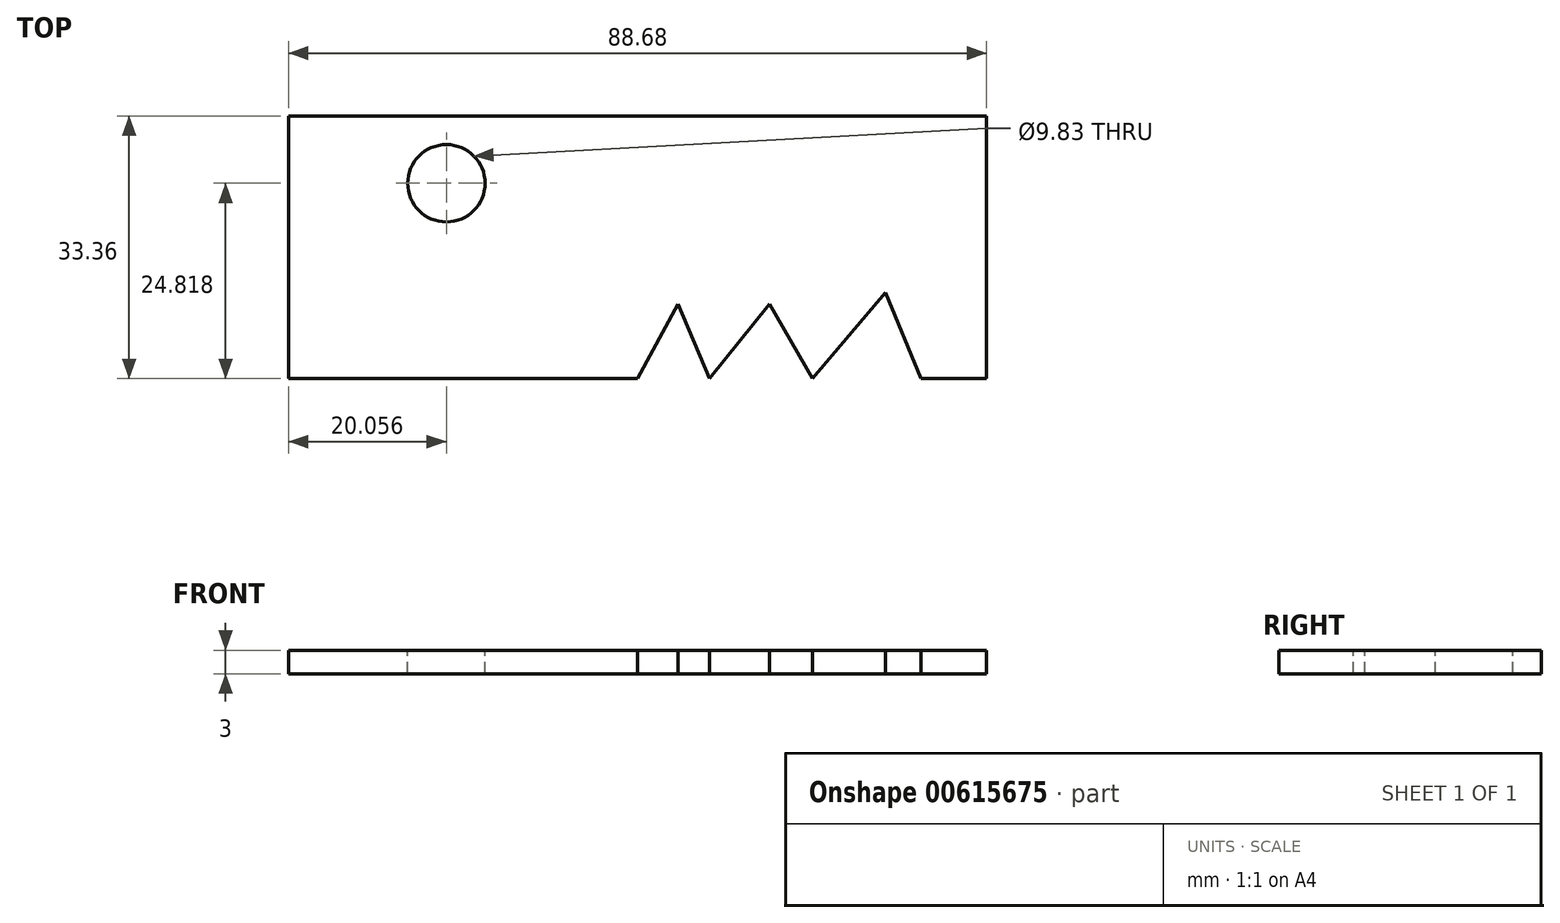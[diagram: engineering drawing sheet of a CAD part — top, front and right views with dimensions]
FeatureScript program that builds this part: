
annotation { "Feature Type Name" : "Feature", "Feature Type Description" : "" }
export const myFeature = defineFeature(function(context is Context, id is Id, definition is map)
    precondition{}
    {
        {
            var Q0;
            Q0=qCreatedBy(makeId("Top.planeOp"),FACE);
            var sketch = newSketch(context, id + "F0", { "sketchPlane" : qUnion([Q0])});
            skLineSegment(sketch, "E0.bottom", {"start": v(-44.34, 16.68) * mm, "end": v(44.34, 16.68) * mm});
            skLineSegment(sketch, "E0.top", {"start": v(-44.34, -16.68) * mm, "end": v(44.34, -16.68) * mm});
            skLineSegment(sketch, "E0.left", {"start": v(-44.34, 16.68) * mm, "end": v(-44.34, -16.68) * mm});
            skLineSegment(sketch, "E0.right", {"start": v(44.34, 16.68) * mm, "end": v(44.34, -16.68) * mm});
            skPoint(sketch, "E0.middle", {"position": v(0, 0) * mm});
            skSolve(sketch);
        }
        {
            var Q0;
            Q0 = qSketchRegion(id + "F0", true);
            extrude(context, id + "F1", {"entities" : qUnion([Q0]), "depth" : 3 * mm, "offsetDistance" : 25 * mm});
        }
        {
            var Q0;
            Q0=makeQuery(id+"F1.opExtrude","CAP_FACE",FACE,{"disambiguationData":[OSD([sQuery(id+"F0.wireOp",EDGE,"E0.bottom"),sQuery(id+"F0.wireOp",EDGE,"E0.top"),sQuery(id+"F0.wireOp",EDGE,"E0.left"),sQuery(id+"F0.wireOp",EDGE,"E0.right")])],"isStart":false});
            var sketch = newSketch(context, id + "F2", { "sketchPlane" : qUnion([Q0])});
            skCircle(sketch, "E1", {"center": v(-24.28, 8.14) * mm, "radius": 4.91 * mm});
            skPoint(sketch, "E1.first.point", {"position": v(-28.94, 9.7) * mm});
            skPoint(sketch, "E1.second.point", {"position": v(-19.5, 6.99) * mm});
            skPoint(sketch, "E1.third.point", {"position": v(-27.3, 4.26) * mm});
            skSolve(sketch);
        }
        {
            var Q0;
            Q0=makeQuery(id+"F2.imprint","IMPRINT",FACE,{"disambiguationData":[TD([[makeQuery(id+"F2.imprint","IMPRINT",EDGE,{"derivedFrom":sQuery(id+"F2.wireOp",EDGE,"E1")}),1.0]])]});
            extrude(context, id + "F3", {"entities" : qUnion([Q0]), "operationType" : NewBodyOperationType.REMOVE, "oppositeDirection" : true, "depth" : 25 * mm, "offsetDistance" : 25 * mm});
        }
        {
            var Q0;
            Q0=makeQuery(id+"F1.opExtrude","CAP_FACE",FACE,{"disambiguationData":[OSD([sQuery(id+"F0.wireOp",EDGE,"E0.bottom"),sQuery(id+"F0.wireOp",EDGE,"E0.top"),sQuery(id+"F0.wireOp",EDGE,"E0.left"),sQuery(id+"F0.wireOp",EDGE,"E0.right")])],"isStart":false});
            var sketch = newSketch(context, id + "F4", { "sketchPlane" : qUnion([Q0])});
            skLineSegment(sketch, "E2", {"start": v(0, -16.68) * mm, "end": v(5.17, -7.17) * mm});
            skLineSegment(sketch, "E3", {"start": v(5.17, -7.17) * mm, "end": v(9.16, -16.68) * mm});
            skLineSegment(sketch, "E4", {"start": v(9.16, -16.68) * mm, "end": v(16.78, -7.17) * mm});
            skLineSegment(sketch, "E5", {"start": v(16.78, -7.17) * mm, "end": v(22.23, -16.68) * mm});
            skLineSegment(sketch, "E6", {"start": v(22.23, -16.68) * mm, "end": v(31.48, -5.72) * mm});
            skLineSegment(sketch, "E7", {"start": v(31.48, -5.72) * mm, "end": v(36.02, -16.68) * mm});
            skLineSegment(sketch, "E8", {"start": v(0, -16.68) * mm, "end": v(18.78, -48) * mm});
            skLineSegment(sketch, "E9", {"start": v(36.02, -16.68) * mm, "end": v(18.78, -48) * mm});
            skSolve(sketch);
        }
        {
            var Q0;
            Q0 = qSketchRegion(id + "F4", true);
            extrude(context, id + "F5", {"entities" : qUnion([Q0]), "operationType" : NewBodyOperationType.REMOVE, "oppositeDirection" : true, "depth" : 25 * mm, "offsetDistance" : 25 * mm});
        }
    });
